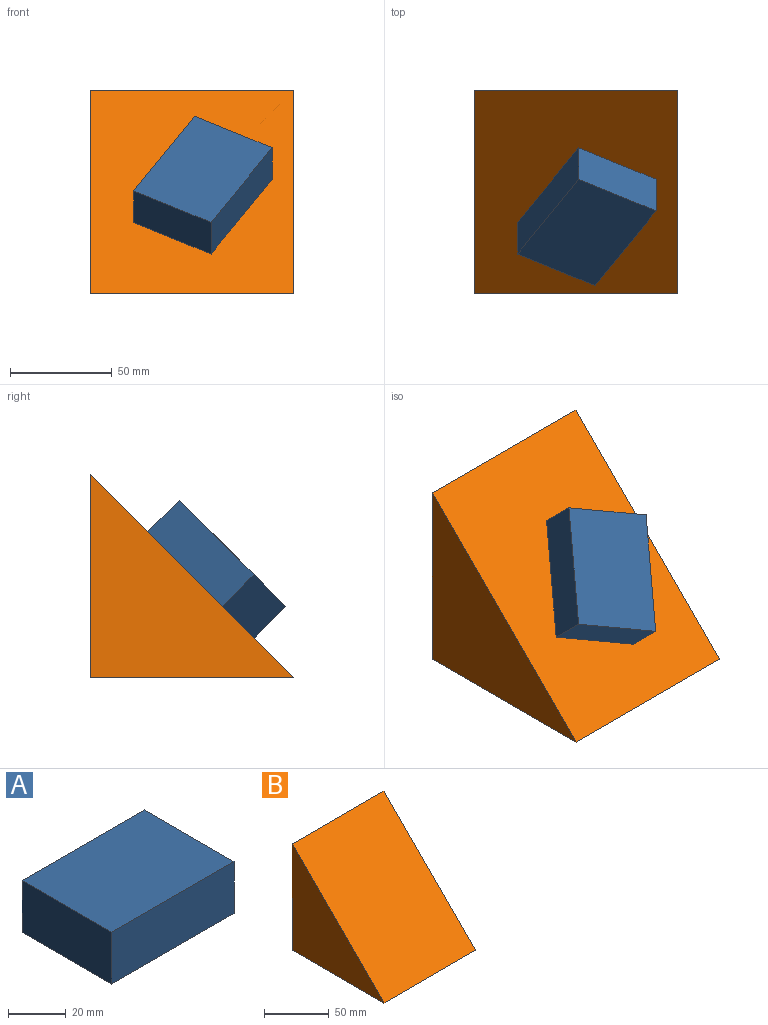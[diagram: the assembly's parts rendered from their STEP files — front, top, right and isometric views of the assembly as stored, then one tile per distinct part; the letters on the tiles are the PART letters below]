
ASSEMBLY  parts=2 mates=1
PART A: 6 faces, bbox 60x44x22 mm
  f0: plane 60x22mm, normal (0,-1,0), area 1320mm2, adj f1,f3,f4,f5
  f1: plane 44x22mm, normal (1,0,0), area 968mm2, adj f0,f2,f4,f5
  f2: plane 60x22mm, normal (0,1,0), area 1320mm2, adj f1,f3,f4,f5
  f3: plane 44x22mm, normal (-1,0,0), area 968mm2, adj f0,f2,f4,f5
  f4: plane 60x44mm, normal (0,0,1), area 2640mm2, adj f0,f1,f2,f3
  f5: plane 60x44mm, normal (0,0,-1), area 2640mm2, adj f0,f1,f2,f3
PART B: 5 faces, bbox 100x100x100 mm
  f0: plane 100x100mm, normal (0,-0.71,0.71), area 14142.1mm2, adj f1,f2,f3,f4
  f1: plane 100x100mm, normal (0,0,-1), area 10000mm2, adj f0,f2,f3,f4
  f2: plane 100x100mm, normal (0,1,0), area 10000mm2, adj f0,f1,f3,f4
  f3: plane 100x100mm, normal (1,0,0), area 5000mm2, adj f0,f1,f2
  f4: plane 100x100mm, normal (-1,0,0), area 5000mm2, adj f0,f1,f2
PLACE A rot(axis=(0.22,0.37,-0.9),125deg) t=(5.34,-12.15,53.4)mm
PLACE B rot(axis=(0,-0.71,0.71),180deg) t=(0,50,50)mm
MATE planar A.f5 <-> B.f0  axis (0,0.71,-0.71) through (5.34,-4.37,45.63)mm
